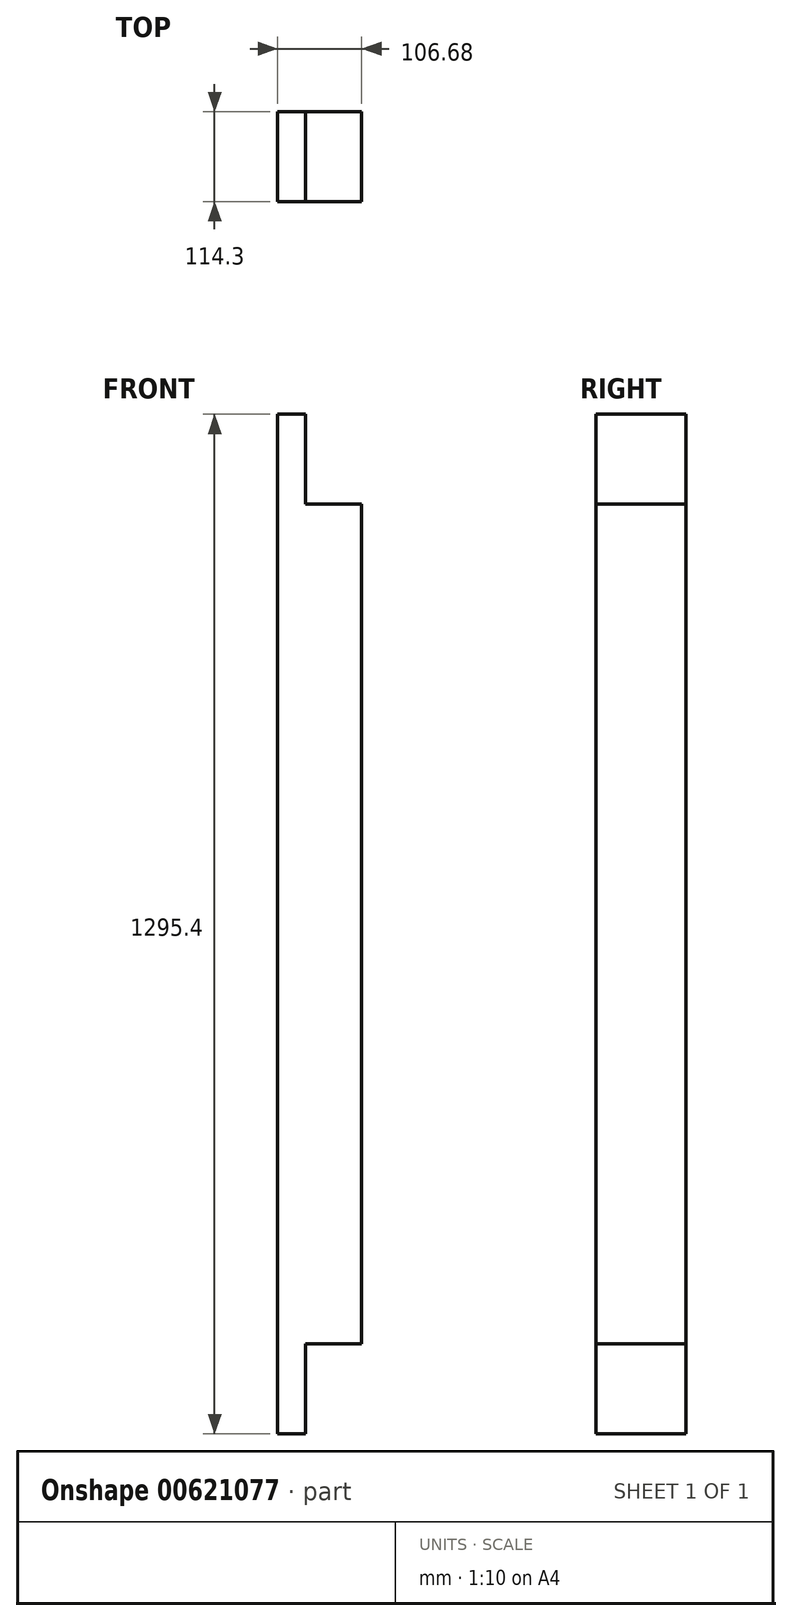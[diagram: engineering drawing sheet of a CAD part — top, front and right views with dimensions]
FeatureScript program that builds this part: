
annotation { "Feature Type Name" : "Feature", "Feature Type Description" : "" }
export const myFeature = defineFeature(function(context is Context, id is Id, definition is map)
    precondition{}
    {
        {
            var Q0;
            Q0=qCreatedBy(makeId("Top.planeOp"),FACE);
            var sketch = newSketch(context, id + "F0", { "sketchPlane" : qUnion([Q0])});
            skLineSegment(sketch, "E0.bottom", {"start": v(-17.78, 57.15) * mm, "end": v(17.78, 57.15) * mm});
            skLineSegment(sketch, "E0.top", {"start": v(-17.78, -57.15) * mm, "end": v(17.78, -57.15) * mm});
            skLineSegment(sketch, "E0.left", {"start": v(-17.78, 57.15) * mm, "end": v(-17.78, -57.15) * mm});
            skLineSegment(sketch, "E0.right", {"start": v(17.78, 57.15) * mm, "end": v(17.78, -57.15) * mm});
            skSolve(sketch);
        }
        {
            var Q0;
            Q0 = qSketchRegion(id + "F0", true);
            extrude(context, id + "F1", {"entities" : qUnion([Q0]), "depth" : 1295.4 * mm, "offsetDistance" : 25.4 * mm});
        }
        {
            var Q0;
            Q0=makeQuery(id+"F1.opExtrude","SWEPT_FACE",FACE,{"disambiguationData":[OSD([sQuery(id+"F0.wireOp",EDGE,"E0.right")])]});
            var sketch = newSketch(context, id + "F2", { "sketchPlane" : qUnion([Q0])});
            skLineSegment(sketch, "E1.bottom", {"start": v(-57.15, 1181.1) * mm, "end": v(57.15, 1181.1) * mm});
            skLineSegment(sketch, "E1.top", {"start": v(-57.15, 114.3) * mm, "end": v(57.15, 114.3) * mm});
            skLineSegment(sketch, "E1.left", {"start": v(-57.15, 1181.1) * mm, "end": v(-57.15, 114.3) * mm});
            skLineSegment(sketch, "E1.right", {"start": v(57.15, 1181.1) * mm, "end": v(57.15, 114.3) * mm});
            skSolve(sketch);
        }
        {
            var Q0;
            Q0 = qSketchRegion(id + "F2", true);
            extrude(context, id + "F3", {"entities" : qUnion([Q0]), "operationType" : NewBodyOperationType.ADD, "depth" : 71.12 * mm, "offsetDistance" : 25.4 * mm});
        }
    });
